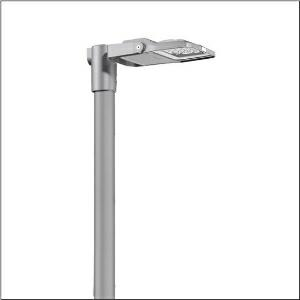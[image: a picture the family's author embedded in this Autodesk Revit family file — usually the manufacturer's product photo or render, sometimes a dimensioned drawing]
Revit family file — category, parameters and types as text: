
# Revit family: floodlight_fl_21_iq_micro___pl64_5xa7761a4e3a_8e2d
name_source: partatom
category: Lighting Fixtures
units: mm (PartAtom-declared; Revit-internal decimal feet)

## family parameters
Cut with Voids When Loaded = No
Host = Face
Light Source = No
Part Type = Normal
Room Calculation Point = No
Round Connector Dimension = Use Diameter
Shared = No

## types (1)
- --- (1 x LED, 2980 lm, 23.1 W, 4000K)
    Apparent Load = 23 VA
    CIE Flux Codes = 28 80 98 100 100
    Color Rendering = 70
    Color Temperature = 4000K
    Default Elevation = 1800 mm
    Description = Floodlight FL 21 iQ micro, floodlight, primary light control with lens, of PMMA, primary optical cover: protective disc, of toughened safety glass, transparent, light distribution: PL64, light emission: direct distribution, installation type: surface-mounted, LED, High Power LED, rated luminous flux: 2.980lm, luminous efficacy: 129lm/W, light colour: 740, colour temperature: 4000K, control gear: iQ Comfort/DALI, control: optimised constant luminous flux control (CLO 2.0), Desk-Remote (wireless, voltage-free reading and setting of iQ features in the workshop via application-optimized NFC function/RFID function), Light-Fading, Smart-Wire, Night-Set, Lumen-Switch, Temp-Guard, Auto-Match, with terminal, 6-pole, mains connection: 220..240V, AC, 50/60Hz, start of lifetime: 23W, end of service life: 24W, reduction: 11W, luminaire housing, of diecast aluminium, powder-coated, Siteco® metallic grey (DB 702S), corrosivity category C5 mid according to DIN EN ISO 12944, suitable for swimming pools, chlorine-resistant, sealing non-destructively replaceable, please order mast flange separately, mast bracket, of steel, galvanised, powder-coated, Siteco® metallic grey (DB 702S), protection rating (complete): IP66, insulation class (complete): insulation class II (safety insulation), certification: CE, ENEC, VDE, protection symbol: D, impact resistance: IK07, permissible operating ambient temperature: -40..+40°C, permissible operating ambient temperature for outdoor applications: -40..+50°C, standard: DIN EN 12944, LABS conformity tested according to VDMA 24364:2018-05, packaging unit: 1 piece

Light Distribution: PL64
    Height = 65 mm
    Lamp = 1 x LED
    Lamp Light Flux = 2980 lm
    Lamp Power = 23.1 W
    Lamp count = 1
    Length = 312 mm
    Luminous efficacy = 129 lm/W
    Manufacturer = Siteco
    ModVariant = No
    Model = 5XA7761A4E3A
    Number of Poles = 1
    OnlyDefault = Yes
    Power Factor = 1
    Product Name = Floodlight FL 21 iQ micro | PL64
    Product group = floodlight | pylon annexe
    ProductGroupID = 6200
    Protection Class = Protection class II
    Protection Degree = IP 66
    RLX_Detail_Level = 1
    RLX_Emergency_Light_Flux = 0 lm
    RLX_Emergency_Type = 0
    RLX_Emergency_Type_DB = No
    RlxData = <blob elided: 101801 chars, md5=5b3cc365>
    Socket = socket
    Standby Power = 0 W
    System Light Flux = 2980 lm
    System Power = 23 W
    Type Comments = factory setting: luminous flux: 100 % | dim-lin: 254 | 455 mA
    Type Image = l_1007121.jpg
    URL = http://relux.com
    VarID = @adj_180722
    Voltage = 0 V
    Weight = 0.00 kg
    Width = 230 mm

## geometry (parser evidence)
native form markers: Blend x4, Sweep x12
no freeform markers — native parametric forms only
